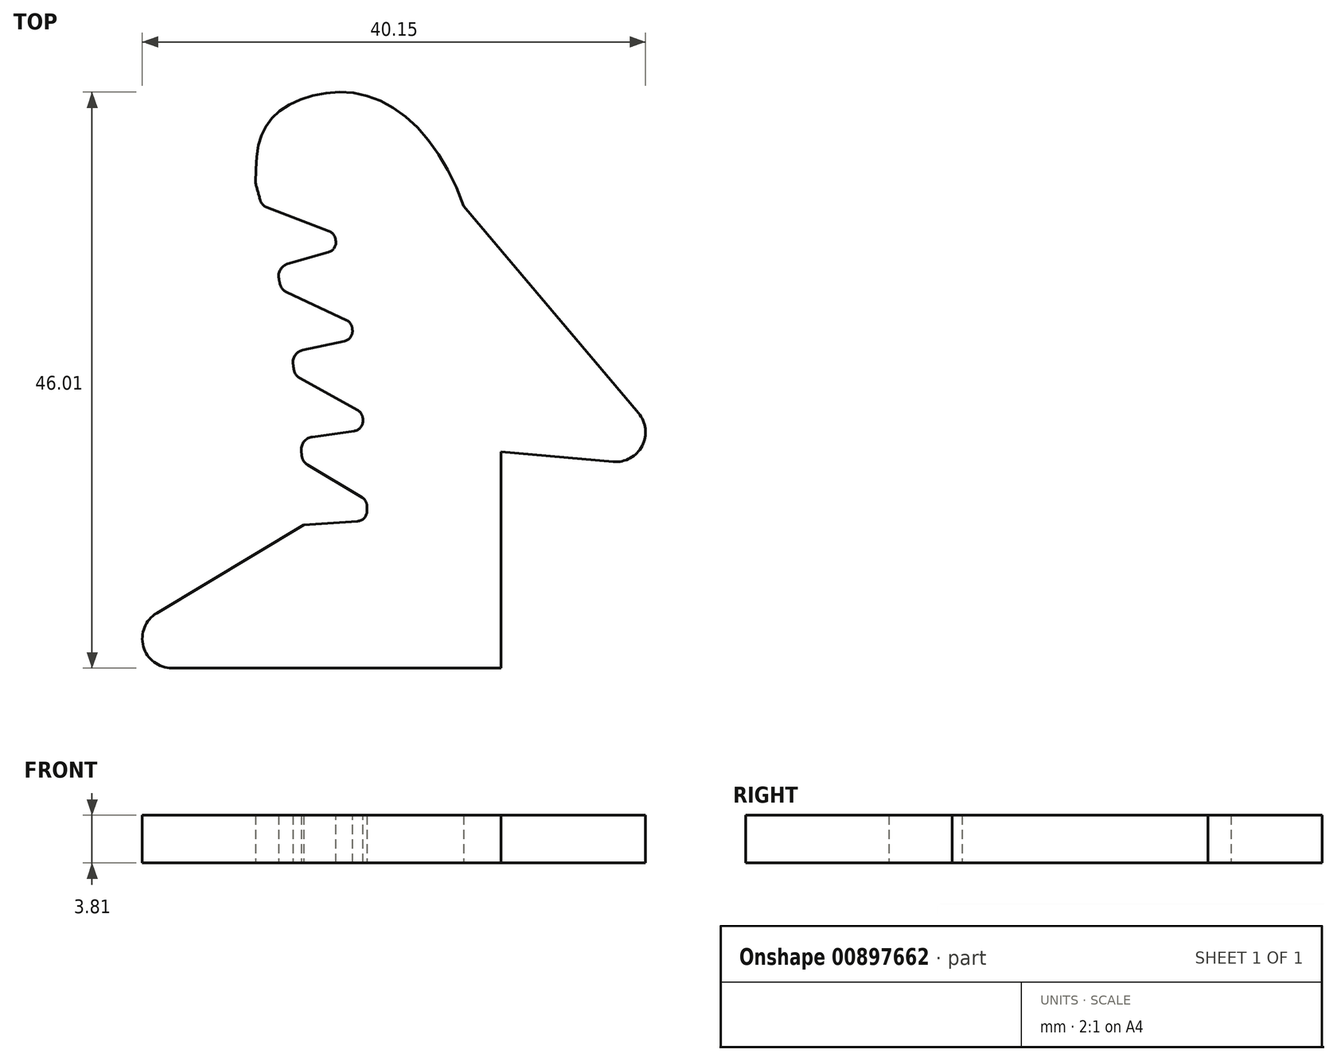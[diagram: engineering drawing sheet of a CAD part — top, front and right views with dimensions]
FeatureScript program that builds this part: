
annotation { "Feature Type Name" : "Feature", "Feature Type Description" : "" }
export const myFeature = defineFeature(function(context is Context, id is Id, definition is map)
    precondition{}
    {
        {
            var Q0;
            Q0=qCreatedBy(makeId("Top.planeOp"),FACE);
            var sketch = newSketch(context, id + "F0", { "sketchPlane" : qUnion([Q0])});
            skLineSegment(sketch, "E0", {"start": v(99.06, -11.43) * mm, "end": v(114.8, -11.43) * mm});
            skCircle(sketch, "E1", {"center": v(0, 0) * mm, "radius": 99.06 * mm});
            skLineSegment(sketch, "E2", {"start": v(99.06, 0) * mm, "end": v(104.13, 0.35) * mm});
            skLineSegment(sketch, "E3", {"start": v(104.13, 0.35) * mm, "end": v(104.13, 1.96) * mm});
            skLineSegment(sketch, "E4", {"start": v(104.13, 1.96) * mm, "end": v(98.93, 5.08) * mm});
            skLineSegment(sketch, "E5", {"start": v(0, 0) * mm, "end": v(26, 0) * mm});
            skLineSegment(sketch, "E6", {"start": v(0, 0) * mm, "end": v(98.82, 6.91) * mm});
            skLineSegment(sketch, "E7", {"start": v(98.82, 6.91) * mm, "end": v(103.85, 7.62) * mm});
            skLineSegment(sketch, "E8", {"start": v(103.85, 7.62) * mm, "end": v(103.76, 8.96) * mm});
            skLineSegment(sketch, "E9", {"start": v(103.76, 8.96) * mm, "end": v(98.33, 11.97) * mm});
            skLineSegment(sketch, "E10", {"start": v(0, 0) * mm, "end": v(98.1, 13.79) * mm});
            skLineSegment(sketch, "E11", {"start": v(98.1, 13.79) * mm, "end": v(103.06, 14.84) * mm});
            skLineSegment(sketch, "E12", {"start": v(103.06, 14.84) * mm, "end": v(102.88, 16.18) * mm});
            skLineSegment(sketch, "E13", {"start": v(102.88, 16.18) * mm, "end": v(97.26, 18.8) * mm});
            skLineSegment(sketch, "E14", {"start": v(0, 0) * mm, "end": v(96.9, 20.6) * mm});
            skLineSegment(sketch, "E15", {"start": v(96.9, 20.6) * mm, "end": v(101.78, 22) * mm});
            skLineSegment(sketch, "E16", {"start": v(101.78, 22) * mm, "end": v(101.5, 23.31) * mm});
            skLineSegment(sketch, "E17", {"start": v(101.5, 23.31) * mm, "end": v(95.71, 25.54) * mm});
            skLineSegment(sketch, "E18", {"start": v(0, 0) * mm, "end": v(95.22, 27.3) * mm});
            skFitSpline(sketch, "E19", {"points": [v(95.22, 27.3) * mm, v(96.74, 32.72) * mm, v(103.73, 34.38) * mm, v(111.84, 25.48) * mm, v(114.8, 5.84) * mm], "startDerivative": vector(0.38, 41.3) * mm, "endDerivative": vector(5.58, -40.57) * mm});
            skLineSegment(sketch, "E20", {"start": v(114.8, -11.43) * mm, "end": v(114.8, 5.84) * mm});
            skLineSegment(sketch, "E21", {"start": v(99.06, -11.43) * mm, "end": v(80.01, -11.43) * mm});
            skLineSegment(sketch, "E22", {"start": v(80.01, -11.43) * mm, "end": v(99.06, 0) * mm});
            skLineSegment(sketch, "E23", {"start": v(114.8, 5.84) * mm, "end": v(129.48, 4.56) * mm});
            skLineSegment(sketch, "E24", {"start": v(129.48, 4.56) * mm, "end": v(111.84, 25.48) * mm});
            skSolve(sketch);
        }
        {
            var Q0;
            {var subQ6=sQuery(id+"F0.wireOp",EDGE,"E0");Q0=makeQuery(id+"F0.imprint","IMPRINT",FACE,{"disambiguationData":[TD([[makeQuery(id+"F0.imprint","IMPRINT",EDGE,{"derivedFrom":subQ6}),1.0]])]});}
            var Q1;
            {var subQ0=sQuery(id+"F0.wireOp",EDGE,"E22");Q1=makeQuery(id+"F0.imprint","IMPRINT",FACE,{"disambiguationData":[TD([[makeQuery(id+"F0.imprint","IMPRINT",EDGE,{"derivedFrom":subQ0}),-1.0]])]});}
            var Q2;
            {var subQ0=sQuery(id+"F0.wireOp",EDGE,"E23");Q2=makeQuery(id+"F0.imprint","IMPRINT",FACE,{"disambiguationData":[TD([[makeQuery(id+"F0.imprint","IMPRINT",EDGE,{"derivedFrom":subQ0}),1.0]])]});}
            extrude(context, id + "F1", {"entities" : qUnion([Q0, Q1, Q2]), "depth" : 3.8 * mm, "offsetDistance" : 25.4 * mm});
        }
        {
            var Q0;
            Q0=makeQuery(id+"F1.opExtrude","SWEPT_EDGE",EDGE,{"disambiguationData":[OSD([sQuery(id+"F0.wireOp",EDGE,"E21"),sQuery(id+"F0.wireOp",EDGE,"E22")])]});
            var Q1;
            Q1=makeQuery(id+"F1.opExtrude","SWEPT_EDGE",EDGE,{"disambiguationData":[OSD([sQuery(id+"F0.wireOp",EDGE,"E23"),sQuery(id+"F0.wireOp",EDGE,"E24")])]});
            fillet(context, id + "F2", {"entities" : qUnion([Q0, Q1]), "radius" : 2.37 * mm, "tangentPropagation" : true, "allowEdgeOverflow" : false});
        }
        {
            var Q0;
            Q0=makeQuery(id+"F1.opExtrude","SWEPT_EDGE",EDGE,{"disambiguationData":[OSD([sQuery(id+"F0.wireOp",EDGE,"E2"),sQuery(id+"F0.wireOp",EDGE,"E3")])]});
            var Q1;
            Q1=makeQuery(id+"F1.opExtrude","SWEPT_EDGE",EDGE,{"disambiguationData":[OSD([sQuery(id+"F0.wireOp",EDGE,"E3"),sQuery(id+"F0.wireOp",EDGE,"E4")])]});
            var Q2;
            Q2=makeQuery(id+"F1.opExtrude","SWEPT_EDGE",EDGE,{"disambiguationData":[OSD([sQuery(id+"F0.wireOp",EDGE,"E7"),sQuery(id+"F0.wireOp",EDGE,"E8")])]});
            var Q3;
            Q3=makeQuery(id+"F1.opExtrude","SWEPT_EDGE",EDGE,{"disambiguationData":[OSD([sQuery(id+"F0.wireOp",EDGE,"E8"),sQuery(id+"F0.wireOp",EDGE,"E9")])]});
            var Q4;
            Q4=makeQuery(id+"F1.opExtrude","SWEPT_EDGE",EDGE,{"disambiguationData":[OSD([sQuery(id+"F0.wireOp",EDGE,"E11"),sQuery(id+"F0.wireOp",EDGE,"E12")])]});
            var Q5;
            Q5=makeQuery(id+"F1.opExtrude","SWEPT_EDGE",EDGE,{"disambiguationData":[OSD([sQuery(id+"F0.wireOp",EDGE,"E12"),sQuery(id+"F0.wireOp",EDGE,"E13")])]});
            var Q6;
            Q6=makeQuery(id+"F1.opExtrude","SWEPT_EDGE",EDGE,{"disambiguationData":[OSD([sQuery(id+"F0.wireOp",EDGE,"E15"),sQuery(id+"F0.wireOp",EDGE,"E16")])]});
            var Q7;
            Q7=makeQuery(id+"F1.opExtrude","SWEPT_EDGE",EDGE,{"disambiguationData":[OSD([sQuery(id+"F0.wireOp",EDGE,"E16"),sQuery(id+"F0.wireOp",EDGE,"E17")])]});
            var Q8;
            Q8=makeQuery(id+"F1.opExtrude","SWEPT_EDGE",EDGE,{"disambiguationData":[OSD([sQuery(id+"F0.wireOp",EDGE,"E1"),sQuery(id+"F0.wireOp",EDGE,"E17")])]});
            fillet(context, id + "F3", {"entities" : qUnion([Q0, Q1, Q2, Q3, Q4, Q5, Q6, Q7, Q8]), "radius" : 0.83 * mm, "tangentPropagation" : true, "allowEdgeOverflow" : false});
        }
        {
            var Q0;
            Q0=makeQuery(id+"F1.opExtrude","SWEPT_EDGE",EDGE,{"disambiguationData":[OSD([sQuery(id+"F0.wireOp",EDGE,"E1"),sQuery(id+"F0.wireOp",EDGE,"E6"),sQuery(id+"F0.wireOp",EDGE,"E7")])]});
            var Q1;
            Q1=makeQuery(id+"F1.opExtrude","SWEPT_EDGE",EDGE,{"disambiguationData":[OSD([sQuery(id+"F0.wireOp",EDGE,"E1"),sQuery(id+"F0.wireOp",EDGE,"E10"),sQuery(id+"F0.wireOp",EDGE,"E11")])]});
            var Q2;
            Q2=makeQuery(id+"F1.opExtrude","SWEPT_EDGE",EDGE,{"disambiguationData":[OSD([sQuery(id+"F0.wireOp",EDGE,"E1"),sQuery(id+"F0.wireOp",EDGE,"E14"),sQuery(id+"F0.wireOp",EDGE,"E15")])]});
            var Q3;
            Q3=makeQuery(id+"F1.opExtrude","SWEPT_EDGE",EDGE,{"disambiguationData":[OSD([sQuery(id+"F0.wireOp",EDGE,"E1"),sQuery(id+"F0.wireOp",EDGE,"E13")])]});
            var Q4;
            Q4=makeQuery(id+"F1.opExtrude","SWEPT_EDGE",EDGE,{"disambiguationData":[OSD([sQuery(id+"F0.wireOp",EDGE,"E1"),sQuery(id+"F0.wireOp",EDGE,"E9")])]});
            var Q5;
            Q5=makeQuery(id+"F1.opExtrude","SWEPT_EDGE",EDGE,{"disambiguationData":[OSD([sQuery(id+"F0.wireOp",EDGE,"E1"),sQuery(id+"F0.wireOp",EDGE,"E4")])]});
            fillet(context, id + "F4", {"entities" : qUnion([Q0, Q1, Q2, Q3, Q4, Q5]), "radius" : 1.02 * mm, "tangentPropagation" : true, "allowEdgeOverflow" : false});
        }
    });
